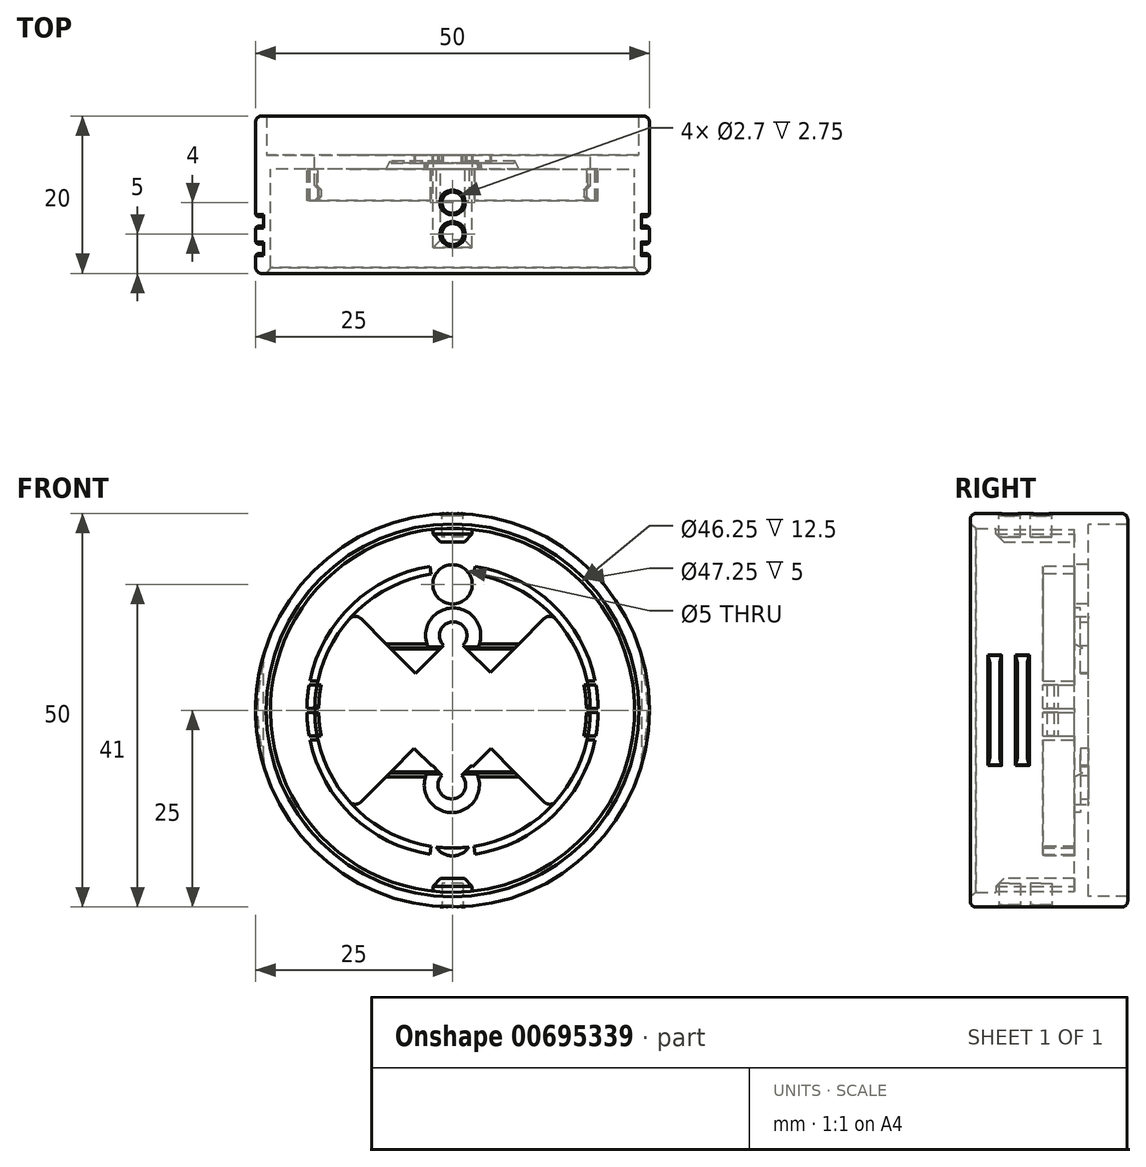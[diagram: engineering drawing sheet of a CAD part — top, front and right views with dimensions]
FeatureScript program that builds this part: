
annotation { "Feature Type Name" : "Feature", "Feature Type Description" : "" }
export const myFeature = defineFeature(function(context is Context, id is Id, definition is map)
    precondition{}
    {
        {
            var Q0;
            Q0=qCreatedBy(makeId("Front.planeOp"),FACE);
            var sketch = newSketch(context, id + "F0", { "sketchPlane" : qUnion([Q0])});
            skCircle(sketch, "E0", {"center": v(0, 0) * mm, "radius": 23.62 * mm});
            skCircle(sketch, "E1", {"center": v(0, 0) * mm, "radius": 25 * mm});
            skArc(sketch, "E2", {"start": v(-12.37, 12.37) * mm, "mid": v(-17.5, 0) * mm, "end": v(-12.37, -12.37) * mm});
            skLineSegment(sketch, "E3.bottom", {"start": v(-1.33, -8.26) * mm, "end": v(-4.8, -4.8) * mm});
            skLineSegment(sketch, "E3.top", {"start": v(4.8, 4.8) * mm, "end": v(1.33, 8.26) * mm});
            skLineSegment(sketch, "E3.left", {"start": v(1.15, -8.26) * mm, "end": v(4.7, -4.7) * mm});
            skLineSegment(sketch, "E3.right", {"start": v(-4.7, 4.7) * mm, "end": v(-1.15, 8.26) * mm});
            skArc(sketch, "E4", {"start": v(1.33, 8.26) * mm, "mid": v(0.1, 11.25) * mm, "end": v(-1.15, 8.26) * mm});
            skArc(sketch, "E5", {"start": v(-1.33, -8.26) * mm, "mid": v(-0.09, -11.25) * mm, "end": v(1.15, -8.26) * mm});
            skLineSegment(sketch, "E6", {"start": v(4.7, -4.7) * mm, "end": v(12.37, -12.37) * mm});
            skLineSegment(sketch, "E7", {"start": v(4.8, 4.8) * mm, "end": v(12.37, 12.37) * mm});
            skLineSegment(sketch, "E8", {"start": v(-4.7, 4.7) * mm, "end": v(-12.37, 12.37) * mm});
            skLineSegment(sketch, "E9", {"start": v(-4.8, -4.8) * mm, "end": v(-12.37, -12.37) * mm});
            skArc(sketch, "E10.trimOffspring", {"start": v(12.37, -12.37) * mm, "mid": v(17.5, 0) * mm, "end": v(12.37, 12.37) * mm});
            skCircle(sketch, "E11", {"center": v(0, 0) * mm, "radius": 23.12 * mm});
            skSolve(sketch);
        }
        {
            var Q0;
            Q0=makeQuery(id+"F0.imprint","IMPRINT",FACE,{"disambiguationData":[TD([[makeQuery(id+"F0.imprint","IMPRINT",EDGE,{"derivedFrom":sQuery(id+"F0.wireOp",EDGE,"E0")}),-1.0]])]});
            var Q1;
            Q1=makeQuery(id+"F0.imprint","IMPRINT",FACE,{"disambiguationData":[TD([[makeQuery(id+"F0.imprint","IMPRINT",EDGE,{"derivedFrom":sQuery(id+"F0.wireOp",EDGE,"E0")}),1.0]])]});
            extrude(context, id + "F1", {"entities" : qUnion([Q0, Q1]), "depth" : 15 * mm, "offsetDistance" : 25 * mm});
        }
        {
            var Q0;
            Q0=makeQuery(id+"F0.imprint","IMPRINT",FACE,{"disambiguationData":[TD([[makeQuery(id+"F0.imprint","IMPRINT",EDGE,{"derivedFrom":sQuery(id+"F0.wireOp",EDGE,"E2")}),-1.0]])]});
            extrude(context, id + "F2", {"entities" : qUnion([Q0]), "operationType" : NewBodyOperationType.ADD, "depth" : 1.75 * mm, "offsetDistance" : 25 * mm});
        }
        {
            var Q0;
            Q0=makeQuery(id+"F0.imprint","IMPRINT",FACE,{"disambiguationData":[TD([[makeQuery(id+"F0.imprint","IMPRINT",EDGE,{"derivedFrom":sQuery(id+"F0.wireOp",EDGE,"E0")}),-1.0]])]});
            extrude(context, id + "F3", {"entities" : qUnion([Q0]), "operationType" : NewBodyOperationType.ADD, "oppositeDirection" : true, "depth" : 5 * mm, "offsetDistance" : 25 * mm});
        }
        {
            var Q0;
            Q0=makeQuery(id+"F2.opExtrude","CAP_FACE",FACE,{"disambiguationData":[OSD([sQuery(id+"F0.wireOp",EDGE,"E0"),sQuery(id+"F0.wireOp",EDGE,"E2"),sQuery(id+"F0.wireOp",EDGE,"E3.bottom"),sQuery(id+"F0.wireOp",EDGE,"E3.top"),sQuery(id+"F0.wireOp",EDGE,"E3.left"),sQuery(id+"F0.wireOp",EDGE,"E3.right"),sQuery(id+"F0.wireOp",EDGE,"E4"),sQuery(id+"F0.wireOp",EDGE,"E5"),sQuery(id+"F0.wireOp",EDGE,"E6"),sQuery(id+"F0.wireOp",EDGE,"E7"),sQuery(id+"F0.wireOp",EDGE,"E8"),sQuery(id+"F0.wireOp",EDGE,"E9"),sQuery(id+"F0.wireOp",EDGE,"E10.trimOffspring")])],"isStart":false});
            var sketch = newSketch(context, id + "F4", { "sketchPlane" : qUnion([Q0])});
            skCircle(sketch, "E12", {"center": v(0.1, 9.5) * mm, "radius": 3.5 * mm});
            skCircle(sketch, "E13", {"center": v(-0.09, -9.5) * mm, "radius": 3.5 * mm});
            skSolve(sketch);
        }
        {
            var Q0;
            Q0 = qSketchRegion(id + "F4", true);
            extrude(context, id + "F5", {"entities" : qUnion([Q0]), "operationType" : NewBodyOperationType.REMOVE, "oppositeDirection" : true, "depth" : .75 * mm, "offsetDistance" : 25 * mm});
        }
        {
            var Q0;
            Q0=makeQuery(id+"F2.opExtrude","CAP_FACE",FACE,{"disambiguationData":[OSD([sQuery(id+"F0.wireOp",EDGE,"E0"),sQuery(id+"F0.wireOp",EDGE,"E2"),sQuery(id+"F0.wireOp",EDGE,"E3.bottom"),sQuery(id+"F0.wireOp",EDGE,"E3.top"),sQuery(id+"F0.wireOp",EDGE,"E3.left"),sQuery(id+"F0.wireOp",EDGE,"E3.right"),sQuery(id+"F0.wireOp",EDGE,"E4"),sQuery(id+"F0.wireOp",EDGE,"E5"),sQuery(id+"F0.wireOp",EDGE,"E6"),sQuery(id+"F0.wireOp",EDGE,"E7"),sQuery(id+"F0.wireOp",EDGE,"E8"),sQuery(id+"F0.wireOp",EDGE,"E9"),sQuery(id+"F0.wireOp",EDGE,"E10.trimOffspring")])],"isStart":false});
            var sketch = newSketch(context, id + "F6", { "sketchPlane" : qUnion([Q0])});
            skCircle(sketch, "E14", {"center": v(0, 0) * mm, "radius": 17.5 * mm});
            skArc(sketch, "E15", {"start": v(18.12, 3.75) * mm, "mid": v(0, 18.5) * mm, "end": v(-18.12, 3.75) * mm});
            skLineSegment(sketch, "E16", {"start": v(-18.21, 3.25) * mm, "end": v(-17.2, 3.25) * mm});
            skLineSegment(sketch, "E17", {"start": v(-18.12, 3.75) * mm, "end": v(-17.1, 3.75) * mm});
            skLineSegment(sketch, "E18.MirrorCS", {"start": v(-18.21, -3.25) * mm, "end": v(-17.2, -3.25) * mm});
            skLineSegment(sketch, "E19.MirrorCS", {"start": v(-18.12, -3.75) * mm, "end": v(-17.1, -3.75) * mm});
            skLineSegment(sketch, "E20.trimOffspring", {"start": v(-17.5, 0.25) * mm, "end": v(-18.5, 0.25) * mm});
            skLineSegment(sketch, "E21.trimOffspring", {"start": v(-17.5, -0.25) * mm, "end": v(-18.5, -0.25) * mm});
            skLineSegment(sketch, "E22", {"start": v(0, 0) * mm, "end": v(0, 1.2) * mm});
            skLineSegment(sketch, "E23.MirrorCS", {"start": v(18.12, 3.75) * mm, "end": v(17.1, 3.75) * mm});
            skLineSegment(sketch, "E24.MirrorCS", {"start": v(18.21, 3.25) * mm, "end": v(17.2, 3.25) * mm});
            skLineSegment(sketch, "E25.MirrorCS", {"start": v(17.5, 0.25) * mm, "end": v(18.5, 0.25) * mm});
            skLineSegment(sketch, "E26.MirrorCS", {"start": v(17.5, -0.25) * mm, "end": v(18.5, -0.25) * mm});
            skLineSegment(sketch, "E27.MirrorCS", {"start": v(18.21, -3.25) * mm, "end": v(17.2, -3.25) * mm});
            skLineSegment(sketch, "E28.MirrorCS", {"start": v(18.12, -3.75) * mm, "end": v(17.1, -3.75) * mm});
            skArc(sketch, "E29.trimOffspring", {"start": v(18.5, 0.25) * mm, "mid": v(18.42, 1.76) * mm, "end": v(18.21, 3.25) * mm});
            skArc(sketch, "E30.trimOffspring", {"start": v(18.21, -3.25) * mm, "mid": v(18.42, -1.76) * mm, "end": v(18.5, -0.25) * mm});
            skArc(sketch, "E31.trimOffspring", {"start": v(-18.21, 3.25) * mm, "mid": v(-18.42, 1.76) * mm, "end": v(-18.5, 0.25) * mm});
            skArc(sketch, "E32.trimOffspring", {"start": v(-18.5, -0.25) * mm, "mid": v(-18.42, -1.76) * mm, "end": v(-18.21, -3.25) * mm});
            skArc(sketch, "E33.trimOffspring", {"start": v(-18.12, -3.75) * mm, "mid": v(0, -18.5) * mm, "end": v(18.12, -3.75) * mm});
            skSolve(sketch);
        }
        {
            var Q0;
            Q0=makeQuery(id+"F6.imprint","IMPRINT",FACE,{"disambiguationData":[TD([[makeQuery(id+"F6.imprint","IMPRINT",EDGE,{"derivedFrom":sQuery(id+"F6.wireOp",EDGE,"E15")}),1.0]])]});
            var Q1;
            {var subQ0=sQuery(id+"F6.wireOp",EDGE,"E24.MirrorCS");Q1=makeQuery(id+"F6.imprint","IMPRINT",FACE,{"disambiguationData":[TD([[makeQuery(id+"F6.imprint","IMPRINT",EDGE,{"derivedFrom":subQ0}),1.0]])]});}
            var Q2;
            {var subQ0=sQuery(id+"F6.wireOp",EDGE,"E26.MirrorCS");Q2=makeQuery(id+"F6.imprint","IMPRINT",FACE,{"disambiguationData":[TD([[makeQuery(id+"F6.imprint","IMPRINT",EDGE,{"derivedFrom":subQ0}),-1.0]])]});}
            var Q3;
            {var subQ0=sQuery(id+"F6.wireOp",EDGE,"E19.MirrorCS");Q3=makeQuery(id+"F6.imprint","IMPRINT",FACE,{"disambiguationData":[TD([[makeQuery(id+"F6.imprint","IMPRINT",EDGE,{"derivedFrom":subQ0}),-1.0]])]});}
            var Q4;
            {var subQ0=sQuery(id+"F6.wireOp",EDGE,"E16");Q4=makeQuery(id+"F6.imprint","IMPRINT",FACE,{"disambiguationData":[TD([[makeQuery(id+"F6.imprint","IMPRINT",EDGE,{"derivedFrom":subQ0}),-1.0]])]});}
            var Q5;
            {var subQ0=sQuery(id+"F6.wireOp",EDGE,"E18.MirrorCS");Q5=makeQuery(id+"F6.imprint","IMPRINT",FACE,{"disambiguationData":[TD([[makeQuery(id+"F6.imprint","IMPRINT",EDGE,{"derivedFrom":subQ0}),1.0]])]});}
            extrude(context, id + "F7", {"entities" : qUnion([Q0, Q1, Q2, Q3, Q4, Q5]), "operationType" : NewBodyOperationType.ADD, "depth" : 4 * mm, "offsetDistance" : 25 * mm});
        }
        {
            var Q0;
            {var subQ11=sQuery(id+"F0.wireOp",EDGE,"E7");var subQ14=sQuery(id+"F0.wireOp",EDGE,"E8");var subQ16=sQuery(id+"F0.wireOp",EDGE,"E2");var subQ17=sQuery(id+"F0.wireOp",EDGE,"E10.trimOffspring");var subQ19=sQuery(id+"F0.wireOp",EDGE,"E11");var subQ20=sQuery(id+"F0.wireOp",EDGE,"E9");var subQ22=sQuery(id+"F0.wireOp",EDGE,"E6");Q0=makeQuery(id+"F7.boolean.opBoolean","SPLIT",FACE,{"disambiguationData":[TD([makeQuery(id+"F1.opExtrude","SWEPT_FACE",FACE,{"disambiguationData":[OSD([subQ19])]})])],"derivedFrom":makeQuery(id+"F2.opExtrude","CAP_FACE",FACE,{"disambiguationData":[OSD([subQ16,sQuery(id+"F0.wireOp",EDGE,"E3.bottom"),sQuery(id+"F0.wireOp",EDGE,"E3.top"),sQuery(id+"F0.wireOp",EDGE,"E3.left"),sQuery(id+"F0.wireOp",EDGE,"E3.right"),sQuery(id+"F0.wireOp",EDGE,"E4"),sQuery(id+"F0.wireOp",EDGE,"E5"),subQ22,subQ11,subQ14,subQ20,subQ17,subQ19])],"isStart":false})});}
            var sketch = newSketch(context, id + "F8", { "sketchPlane" : qUnion([Q0])});
            skLineSegment(sketch, "E34.bottom", {"start": v(2.5, 21.37) * mm, "end": v(-2.5, 21.37) * mm});
            skLineSegment(sketch, "E34.top", {"start": v(2.5, 24.87) * mm, "end": v(-2.5, 24.87) * mm});
            skLineSegment(sketch, "E34.left", {"start": v(2.5, 21.37) * mm, "end": v(2.5, 24.87) * mm});
            skLineSegment(sketch, "E34.right", {"start": v(-2.5, 21.37) * mm, "end": v(-2.5, 24.87) * mm});
            skPoint(sketch, "E34.middle", {"position": v(0, 23.12) * mm});
            skCircle(sketch, "E35", {"center": v(0, 0) * mm, "radius": 23.12 * mm});
            skLineSegment(sketch, "E36", {"start": v(0, 0) * mm, "end": v(4.23, 0) * mm});
            skLineSegment(sketch, "E37.MirrorCS", {"start": v(-7.5, 21.37) * mm, "end": v(-2.5, 21.37) * mm});
            skLineSegment(sketch, "E38.MirrorCS", {"start": v(-7.5, 21.37) * mm, "end": v(-7.5, 24.87) * mm});
            skLineSegment(sketch, "E39.MirrorCS", {"start": v(-2.5, -21.37) * mm, "end": v(-2.5, -24.87) * mm});
            skLineSegment(sketch, "E40.MirrorCS", {"start": v(2.5, -21.37) * mm, "end": v(2.5, -24.87) * mm});
            skLineSegment(sketch, "E41.MirrorCS", {"start": v(2.5, -21.37) * mm, "end": v(-2.5, -21.37) * mm});
            skLineSegment(sketch, "E42.MirrorCS", {"start": v(2.5, -24.87) * mm, "end": v(-2.5, -24.87) * mm});
            skSolve(sketch);
        }
        {
            var Q0;
            {var subQ0=sQuery(id+"F8.wireOp",EDGE,"E34.bottom");Q0=makeQuery(id+"F8.imprint","IMPRINT",FACE,{"disambiguationData":[TD([[makeQuery(id+"F8.imprint","IMPRINT",EDGE,{"derivedFrom":subQ0}),-1.0]])]});}
            var Q1;
            {var subQ5=sQuery(id+"F8.wireOp",EDGE,"E41.MirrorCS");Q1=makeQuery(id+"F8.imprint","IMPRINT",FACE,{"disambiguationData":[TD([[makeQuery(id+"F8.imprint","IMPRINT",EDGE,{"derivedFrom":subQ5}),1.0]])]});}
            extrude(context, id + "F9", {"entities" : qUnion([Q0, Q1]), "operationType" : NewBodyOperationType.ADD, "depth" : 10 * mm, "offsetDistance" : 25 * mm});
        }
        {
            var Q0;
            Q0=makeQuery(id+"F2.opExtrude","CAP_FACE",FACE,{"disambiguationData":[OSD([sQuery(id+"F0.wireOp",EDGE,"E0"),sQuery(id+"F0.wireOp",EDGE,"E2"),sQuery(id+"F0.wireOp",EDGE,"E3.bottom"),sQuery(id+"F0.wireOp",EDGE,"E3.top"),sQuery(id+"F0.wireOp",EDGE,"E3.left"),sQuery(id+"F0.wireOp",EDGE,"E3.right"),sQuery(id+"F0.wireOp",EDGE,"E4"),sQuery(id+"F0.wireOp",EDGE,"E5"),sQuery(id+"F0.wireOp",EDGE,"E6"),sQuery(id+"F0.wireOp",EDGE,"E7"),sQuery(id+"F0.wireOp",EDGE,"E8"),sQuery(id+"F0.wireOp",EDGE,"E9"),sQuery(id+"F0.wireOp",EDGE,"E10.trimOffspring")])],"isStart":false});
            var sketch = newSketch(context, id + "F10", { "sketchPlane" : qUnion([Q0])});
            skLineSegment(sketch, "E43.bottom", {"start": v(9.72, 0) * mm, "end": v(0, -9.72) * mm});
            skLineSegment(sketch, "E43.top", {"start": v(0, 9.72) * mm, "end": v(-9.72, 0) * mm});
            skLineSegment(sketch, "E43.left", {"start": v(9.72, 0) * mm, "end": v(0, 9.72) * mm});
            skLineSegment(sketch, "E43.right", {"start": v(0, -9.72) * mm, "end": v(-9.72, 0) * mm});
            skPoint(sketch, "E43.middle", {"position": v(0, 0) * mm});
            skSolve(sketch);
        }
        {
            var Q0;
            Q0=makeQuery(id+"F7.opExtrude","CAP_FACE",FACE,{"disambiguationData":[OSD([sQuery(id+"F6.wireOp",EDGE,"E14"),sQuery(id+"F6.wireOp",EDGE,"E15"),sQuery(id+"F6.wireOp",EDGE,"E17"),sQuery(id+"F6.wireOp",EDGE,"E23.MirrorCS")])],"isStart":false});
            var sketch = newSketch(context, id + "F11", { "sketchPlane" : qUnion([Q0])});
            skArc(sketch, "E44", {"start": v(-16.69, 3.25) * mm, "mid": v(-16.9, 1.76) * mm, "end": v(-17, 0.25) * mm});
            skLineSegment(sketch, "E45", {"start": v(-17.7, 3.25) * mm, "end": v(-16.69, 3.25) * mm});
            skLineSegment(sketch, "E46", {"start": v(-18, 0.25) * mm, "end": v(-17, 0.25) * mm});
            skLineSegment(sketch, "E47", {"start": v(-18, -0.25) * mm, "end": v(-17, -0.25) * mm});
            skLineSegment(sketch, "E48", {"start": v(-17.7, -3.25) * mm, "end": v(-16.69, -3.25) * mm});
            skArc(sketch, "E49.trimOffspring", {"start": v(-17, -0.25) * mm, "mid": v(-16.9, -1.76) * mm, "end": v(-16.69, -3.25) * mm});
            skLineSegment(sketch, "E50", {"start": v(0, 0) * mm, "end": v(0, 1.46) * mm});
            skLineSegment(sketch, "E51.MirrorCS", {"start": v(18, -0.25) * mm, "end": v(17, -0.25) * mm});
            skLineSegment(sketch, "E52.MirrorCS", {"start": v(17.7, -3.25) * mm, "end": v(16.69, -3.25) * mm});
            skLineSegment(sketch, "E53.MirrorCS", {"start": v(18, 0.25) * mm, "end": v(17, 0.25) * mm});
            skArc(sketch, "E54.MirrorCS", {"start": v(17.7, 3.25) * mm, "mid": v(17.91, 1.76) * mm, "end": v(18, 0.25) * mm});
            skArc(sketch, "E55.MirrorCS", {"start": v(16.69, 3.25) * mm, "mid": v(16.9, 1.76) * mm, "end": v(17, 0.25) * mm});
            skArc(sketch, "E56.MirrorCS", {"start": v(18, -0.25) * mm, "mid": v(17.92, -1.76) * mm, "end": v(17.7, -3.25) * mm});
            skLineSegment(sketch, "E57.MirrorCS", {"start": v(17.7, 3.25) * mm, "end": v(16.69, 3.25) * mm});
            skArc(sketch, "E58.MirrorCS", {"start": v(17, -0.25) * mm, "mid": v(16.9, -1.76) * mm, "end": v(16.69, -3.25) * mm});
            skLineSegment(sketch, "E59", {"start": v(-17.7, 3.25) * mm, "end": v(-18, 0.25) * mm});
            skLineSegment(sketch, "E60", {"start": v(-18, -0.25) * mm, "end": v(-17.7, -3.25) * mm});
            skLineSegment(sketch, "E61.MirrorCS", {"start": v(18, -0.25) * mm, "end": v(17.7, -3.25) * mm});
            skLineSegment(sketch, "E62.MirrorCS", {"start": v(17.7, 3.25) * mm, "end": v(18, 0.25) * mm});
            skSolve(sketch);
        }
        {
            var Q0;
            Q0=makeQuery(id+"F11.imprint","IMPRINT",FACE,{"disambiguationData":[TD([[makeQuery(id+"F11.imprint","IMPRINT",EDGE,{"derivedFrom":sQuery(id+"F11.wireOp",EDGE,"E47")}),-1.0]])]});
            var Q1;
            Q1=makeQuery(id+"F11.imprint","IMPRINT",FACE,{"disambiguationData":[TD([[makeQuery(id+"F11.imprint","IMPRINT",EDGE,{"derivedFrom":sQuery(id+"F11.wireOp",EDGE,"E44")}),-1.0]])]});
            var Q2;
            Q2=makeQuery(id+"F11.imprint","IMPRINT",FACE,{"disambiguationData":[TD([[makeQuery(id+"F11.imprint","IMPRINT",EDGE,{"derivedFrom":sQuery(id+"F11.wireOp",EDGE,"E57.MirrorCS")}),1.0]])]});
            var Q3;
            Q3=makeQuery(id+"F11.imprint","IMPRINT",FACE,{"disambiguationData":[TD([[makeQuery(id+"F11.imprint","IMPRINT",EDGE,{"derivedFrom":sQuery(id+"F11.wireOp",EDGE,"E52.MirrorCS")}),-1.0]])]});
            extrude(context, id + "F12", {"entities" : qUnion([Q0, Q1, Q2, Q3]), "operationType" : NewBodyOperationType.ADD, "oppositeDirection" : true, "depth" : 1.9 * mm, "offsetDistance" : 25 * mm});
        }
        {
            var Q0;
            Q0=makeQuery(id+"F12.opExtrude","CAP_EDGE",EDGE,{"disambiguationData":[OSD([sQuery(id+"F11.wireOp",EDGE,"E44")])],"isStart":true});
            var Q1;
            Q1=makeQuery(id+"F12.opExtrude","CAP_EDGE",EDGE,{"disambiguationData":[OSD([sQuery(id+"F11.wireOp",EDGE,"E49.trimOffspring")])],"isStart":true});
            var Q2;
            Q2=makeQuery(id+"F12.opExtrude","CAP_EDGE",EDGE,{"disambiguationData":[OSD([sQuery(id+"F11.wireOp",EDGE,"E55.MirrorCS")])],"isStart":true});
            var Q3;
            Q3=makeQuery(id+"F12.opExtrude","CAP_EDGE",EDGE,{"disambiguationData":[OSD([sQuery(id+"F11.wireOp",EDGE,"E58.MirrorCS")])],"isStart":true});
            chamfer(context, id + "F13", {"entities" : qUnion([Q0, Q1, Q2, Q3]), "width" : .5 * mm, "tangentPropagation" : true});
        }
        {
            var Q0;
            Q0=makeQuery(id+"F12.opExtrude","CAP_EDGE",EDGE,{"disambiguationData":[OSD([sQuery(id+"F11.wireOp",EDGE,"E44")])],"isStart":false});
            var Q1;
            Q1=makeQuery(id+"F12.opExtrude","CAP_EDGE",EDGE,{"disambiguationData":[OSD([sQuery(id+"F11.wireOp",EDGE,"E49.trimOffspring")])],"isStart":false});
            var Q2;
            Q2=makeQuery(id+"F12.opExtrude","CAP_EDGE",EDGE,{"disambiguationData":[OSD([sQuery(id+"F11.wireOp",EDGE,"E55.MirrorCS")])],"isStart":false});
            var Q3;
            Q3=makeQuery(id+"F12.opExtrude","CAP_EDGE",EDGE,{"disambiguationData":[OSD([sQuery(id+"F11.wireOp",EDGE,"E58.MirrorCS")])],"isStart":false});
            chamfer(context, id + "F14", {"entities" : qUnion([Q0, Q1, Q2, Q3]), "width" : .5 * mm, "tangentPropagation" : true});
        }
        {
            var Q0;
            Q0=qCreatedBy(makeId("Top.planeOp"),FACE);
            cPlane(context, id + "F15", {"entities" : qUnion([Q0]), "cplaneType" : CPlaneType.OFFSET, "offset" : 25 * mm, "width" : 150 * mm, "height" : 150 * mm});
        }
        {
            var Q0;
            Q0=makeQuery(id+"F1.opExtrude","CAP_FACE",FACE,{"disambiguationData":[OSD([sQuery(id+"F0.wireOp",EDGE,"E0"),sQuery(id+"F0.wireOp",EDGE,"E1")])],"isStart":false});
            var sketch = newSketch(context, id + "F16", { "sketchPlane" : qUnion([Q0])});
            skPoint(sketch, "E63", {"position": v(0, 0) * mm});
            skSolve(sketch);
        }
        {
            var Q0;
            Q0=qCreatedBy(id+"F15.planeOp",FACE);
            var sketch = newSketch(context, id + "F17", { "sketchPlane" : qUnion([Q0])});
            skLineSegment(sketch, "E64", {"start": v(0, -15) * mm, "end": v(0, -10) * mm});
            skCircle(sketch, "E65", {"center": v(0, -10) * mm, "radius": 1.35 * mm});
            skLineSegment(sketch, "E66", {"start": v(0, -15) * mm, "end": v(0, -6) * mm});
            skCircle(sketch, "E67", {"center": v(0, -6) * mm, "radius": 1.35 * mm});
            skSolve(sketch);
        }
        {
            var Q0;
            Q0 = qSketchRegion(id + "F17", true);
            extrude(context, id + "F18", {"entities" : qUnion([Q0]), "operationType" : NewBodyOperationType.REMOVE, "oppositeDirection" : true, "depth" : 3 * mm, "offsetDistance" : 25 * mm});
        }
        {
            var Q0;
            Q0=qCreatedBy(makeId("Top.planeOp"),FACE);
            cPlane(context, id + "F19", {"entities" : qUnion([Q0]), "cplaneType" : CPlaneType.OFFSET, "offset" : 25 * mm, "oppositeDirection" : true, "width" : 150 * mm, "height" : 150 * mm});
        }
        {
            var Q0;
            Q0=qCreatedBy(id+"F19.planeOp",FACE);
            var sketch = newSketch(context, id + "F20", { "sketchPlane" : qUnion([Q0])});
            skLineSegment(sketch, "E68", {"start": v(0, -15) * mm, "end": v(0, -10) * mm});
            skCircle(sketch, "E69", {"center": v(0, -10) * mm, "radius": 1.35 * mm});
            skLineSegment(sketch, "E70", {"start": v(0, -15) * mm, "end": v(0, -6) * mm});
            skCircle(sketch, "E71", {"center": v(0, -6) * mm, "radius": 1.35 * mm});
            skSolve(sketch);
        }
        {
            var Q0;
            Q0 = qSketchRegion(id + "F20", true);
            extrude(context, id + "F21", {"entities" : qUnion([Q0]), "operationType" : NewBodyOperationType.REMOVE, "depth" : 3 * mm, "offsetDistance" : 25 * mm});
        }
        {
            var Q0;
            Q0=qCreatedBy(makeId("Right.planeOp"),FACE);
            cPlane(context, id + "F22", {"entities" : qUnion([Q0]), "cplaneType" : CPlaneType.OFFSET, "offset" : 25 * mm, "width" : 150 * mm, "height" : 150 * mm});
        }
        {
            var Q0;
            Q0=qCreatedBy(id+"F22.planeOp",FACE);
            var sketch = newSketch(context, id + "F23", { "sketchPlane" : qUnion([Q0])});
            skLineSegment(sketch, "E72", {"start": v(-15, 0) * mm, "end": v(-11.88, 0) * mm});
            skLineSegment(sketch, "E73.bottom", {"start": v(-11.26, -25) * mm, "end": v(-12.5, -25) * mm});
            skLineSegment(sketch, "E73.top", {"start": v(-11.25, 25) * mm, "end": v(-12.5, 25) * mm});
            skLineSegment(sketch, "E73.left", {"start": v(-11.26, -25) * mm, "end": v(-11.25, 25) * mm});
            skLineSegment(sketch, "E73.right", {"start": v(-12.5, -25) * mm, "end": v(-12.5, 25) * mm});
            skPoint(sketch, "E73.middle", {"position": v(-11.88, 0) * mm});
            skLineSegment(sketch, "E74.bottom", {"start": v(-9, 25) * mm, "end": v(-7.75, 25) * mm});
            skLineSegment(sketch, "E74.top", {"start": v(-9, -25) * mm, "end": v(-7.75, -25) * mm});
            skLineSegment(sketch, "E74.left", {"start": v(-9, 25) * mm, "end": v(-9, -25) * mm});
            skLineSegment(sketch, "E74.right", {"start": v(-7.75, 25) * mm, "end": v(-7.75, -25) * mm});
            skPoint(sketch, "E74.middle", {"position": v(-8.38, 0) * mm});
            skSolve(sketch);
        }
        {
            var Q0;
            Q0 = qSketchRegion(id + "F23", true);
            extrude(context, id + "F24", {"entities" : qUnion([Q0]), "operationType" : NewBodyOperationType.REMOVE, "oppositeDirection" : true, "depth" : 1 * mm, "offsetDistance" : 25 * mm});
        }
        {
            var Q0;
            Q0=qCreatedBy(makeId("Right.planeOp"),FACE);
            cPlane(context, id + "F25", {"entities" : qUnion([Q0]), "cplaneType" : CPlaneType.OFFSET, "offset" : 25 * mm, "oppositeDirection" : true, "width" : 150 * mm, "height" : 150 * mm});
        }
        {
            var Q0;
            Q0=qCreatedBy(id+"F25.planeOp",FACE);
            var sketch = newSketch(context, id + "F26", { "sketchPlane" : qUnion([Q0])});
            skLineSegment(sketch, "E75", {"start": v(-15, 0) * mm, "end": v(-11.88, 0) * mm});
            skLineSegment(sketch, "E76.bottom", {"start": v(-9, -25) * mm, "end": v(-7.76, -25) * mm});
            skLineSegment(sketch, "E76.top", {"start": v(-9, 25) * mm, "end": v(-7.75, 25) * mm});
            skLineSegment(sketch, "E76.left", {"start": v(-9, -25) * mm, "end": v(-9, 25) * mm});
            skLineSegment(sketch, "E76.right", {"start": v(-7.76, -25) * mm, "end": v(-7.75, 25) * mm});
            skPoint(sketch, "E76.middle", {"position": v(-8.38, 0) * mm});
            skLineSegment(sketch, "E77.bottom", {"start": v(-12.5, -25) * mm, "end": v(-11.26, -25) * mm});
            skLineSegment(sketch, "E77.top", {"start": v(-12.5, 25) * mm, "end": v(-11.25, 25) * mm});
            skLineSegment(sketch, "E77.left", {"start": v(-12.5, -25) * mm, "end": v(-12.5, 25) * mm});
            skLineSegment(sketch, "E77.right", {"start": v(-11.26, -25) * mm, "end": v(-11.25, 25) * mm});
            skPoint(sketch, "E77.middle", {"position": v(-11.88, 0) * mm});
            skSolve(sketch);
        }
        {
            var Q0;
            Q0 = qSketchRegion(id + "F26", true);
            extrude(context, id + "F27", {"entities" : qUnion([Q0]), "operationType" : NewBodyOperationType.REMOVE, "depth" : 1 * mm, "offsetDistance" : 25 * mm});
        }
        {
            var Q0;
            Q0=makeQuery(id+"F40.boolean.opBoolean","INTERSECT",EDGE,{"derivedFrom":[makeQuery(id+"F2.opExtrude","SWEPT_FACE",FACE,{"disambiguationData":[OSD([sQuery(id+"F0.wireOp",EDGE,"E8")])]}),makeQuery(id+"F40.opExtrude","SWEPT_FACE",FACE,{"disambiguationData":[OSD([sQuery(id+"F10.wireOp",EDGE,"E43.top")])]})]});
            var Q1;
            Q1=makeQuery(id+"F40.boolean.opBoolean","INTERSECT",EDGE,{"derivedFrom":[makeQuery(id+"F2.opExtrude","SWEPT_FACE",FACE,{"disambiguationData":[OSD([sQuery(id+"F0.wireOp",EDGE,"E7")])]}),makeQuery(id+"F40.opExtrude","SWEPT_FACE",FACE,{"disambiguationData":[OSD([sQuery(id+"F10.wireOp",EDGE,"E43.left")])]})]});
            var Q2;
            Q2=makeQuery(id+"F40.boolean.opBoolean","INTERSECT",EDGE,{"derivedFrom":[makeQuery(id+"F2.opExtrude","SWEPT_FACE",FACE,{"disambiguationData":[OSD([sQuery(id+"F0.wireOp",EDGE,"E6")])]}),makeQuery(id+"F40.opExtrude","SWEPT_FACE",FACE,{"disambiguationData":[OSD([sQuery(id+"F10.wireOp",EDGE,"E43.bottom")])]})]});
            var Q3;
            Q3=makeQuery(id+"F40.boolean.opBoolean","INTERSECT",EDGE,{"derivedFrom":[makeQuery(id+"F2.opExtrude","SWEPT_FACE",FACE,{"disambiguationData":[OSD([sQuery(id+"F0.wireOp",EDGE,"E9")])]}),makeQuery(id+"F40.opExtrude","SWEPT_FACE",FACE,{"disambiguationData":[OSD([sQuery(id+"F10.wireOp",EDGE,"E43.right")])]})]});
            var Q4;
            Q4=makeQuery(id+"F2.opExtrude","SWEPT_EDGE",EDGE,{"disambiguationData":[OSD([sQuery(id+"F0.wireOp",EDGE,"E6"),sQuery(id+"F0.wireOp",EDGE,"E10.trimOffspring")])]});
            var Q5;
            Q5=makeQuery(id+"F2.opExtrude","SWEPT_EDGE",EDGE,{"disambiguationData":[OSD([sQuery(id+"F0.wireOp",EDGE,"E7"),sQuery(id+"F0.wireOp",EDGE,"E10.trimOffspring")])]});
            var Q6;
            Q6=makeQuery(id+"F2.opExtrude","SWEPT_EDGE",EDGE,{"disambiguationData":[OSD([sQuery(id+"F0.wireOp",EDGE,"E2"),sQuery(id+"F0.wireOp",EDGE,"E8")])]});
            var Q7;
            Q7=makeQuery(id+"F2.opExtrude","SWEPT_EDGE",EDGE,{"disambiguationData":[OSD([sQuery(id+"F0.wireOp",EDGE,"E2"),sQuery(id+"F0.wireOp",EDGE,"E9")])]});
            fillet(context, id + "F28", {"entities" : qUnion([Q0, Q1, Q2, Q3, Q4, Q5, Q6, Q7]), "radius" : 1 * mm, "tangentPropagation" : true, "allowEdgeOverflow" : false});
        }
        {
            var Q0;
            Q0=makeQuery(id+"F1.opExtrude","CAP_EDGE",EDGE,{"disambiguationData":[OSD([sQuery(id+"F0.wireOp",EDGE,"E1")])],"isStart":false});
            var Q1;
            Q1=makeQuery(id+"F3.opExtrude","CAP_EDGE",EDGE,{"disambiguationData":[OSD([sQuery(id+"F0.wireOp",EDGE,"E1")])],"isStart":false});
            fillet(context, id + "F29", {"entities" : qUnion([Q0, Q1]), "radius" : .75 * mm, "tangentPropagation" : true, "allowEdgeOverflow" : false});
        }
        {
            var Q0;
            {var subQ0=sQuery(id+"F0.wireOp",EDGE,"E1");Q0=makeQuery(id+"F27.boolean.opBoolean","INTERSECT",EDGE,{"derivedFrom":[makeQuery(id+"F0lZXDNJsSuf2Zf_1.boolean.opBoolean","SPLIT",FACE,{"disambiguationData":[TD([makeQuery(id+"F0lZXDNJsSuf2Zf_1.opExtrude","SWEPT_FACE",FACE,{"disambiguationData":[OSD([sQuery(id+"Fl6joLbU86pnRP5_1.wireOp",EDGE,"838e0230-e5e1-4c86-9a61-0dafe3e3d36a.sketch_text.stroke-0")])]})])],"derivedFrom":makeQuery(id+"F3.boolean.opBoolean","MERGE",FACE,{"derivedFrom":[makeQuery(id+"F1.opExtrude","SWEPT_FACE",FACE,{"disambiguationData":[OSD([subQ0])]}),makeQuery(id+"F3.opExtrude","SWEPT_FACE",FACE,{"disambiguationData":[OSD([subQ0])]})]})}),makeQuery(id+"F27.opExtrude","SWEPT_FACE",FACE,{"disambiguationData":[OSD([sQuery(id+"F26.wireOp",EDGE,"E76.right")])]})]});}
            var Q1;
            {var subQ0=sQuery(id+"F0.wireOp",EDGE,"E1");Q1=makeQuery(id+"F27.boolean.opBoolean","INTERSECT",EDGE,{"derivedFrom":[makeQuery(id+"F0lZXDNJsSuf2Zf_1.boolean.opBoolean","SPLIT",FACE,{"disambiguationData":[TD([makeQuery(id+"F0lZXDNJsSuf2Zf_1.opExtrude","SWEPT_FACE",FACE,{"disambiguationData":[OSD([sQuery(id+"Fl6joLbU86pnRP5_1.wireOp",EDGE,"838e0230-e5e1-4c86-9a61-0dafe3e3d36a.sketch_text.stroke-0")])]})])],"derivedFrom":makeQuery(id+"F3.boolean.opBoolean","MERGE",FACE,{"derivedFrom":[makeQuery(id+"F1.opExtrude","SWEPT_FACE",FACE,{"disambiguationData":[OSD([subQ0])]}),makeQuery(id+"F3.opExtrude","SWEPT_FACE",FACE,{"disambiguationData":[OSD([subQ0])]})]})}),makeQuery(id+"F27.opExtrude","SWEPT_FACE",FACE,{"disambiguationData":[OSD([sQuery(id+"F26.wireOp",EDGE,"E76.left")])]})]});}
            var Q2;
            {var subQ0=sQuery(id+"F0.wireOp",EDGE,"E1");Q2=makeQuery(id+"F27.boolean.opBoolean","INTERSECT",EDGE,{"derivedFrom":[makeQuery(id+"F0lZXDNJsSuf2Zf_1.boolean.opBoolean","SPLIT",FACE,{"disambiguationData":[TD([makeQuery(id+"F0lZXDNJsSuf2Zf_1.opExtrude","SWEPT_FACE",FACE,{"disambiguationData":[OSD([sQuery(id+"Fl6joLbU86pnRP5_1.wireOp",EDGE,"838e0230-e5e1-4c86-9a61-0dafe3e3d36a.sketch_text.stroke-0")])]})])],"derivedFrom":makeQuery(id+"F3.boolean.opBoolean","MERGE",FACE,{"derivedFrom":[makeQuery(id+"F1.opExtrude","SWEPT_FACE",FACE,{"disambiguationData":[OSD([subQ0])]}),makeQuery(id+"F3.opExtrude","SWEPT_FACE",FACE,{"disambiguationData":[OSD([subQ0])]})]})}),makeQuery(id+"F27.opExtrude","SWEPT_FACE",FACE,{"disambiguationData":[OSD([sQuery(id+"F26.wireOp",EDGE,"E77.right")])]})]});}
            var Q3;
            {var subQ0=sQuery(id+"F0.wireOp",EDGE,"E1");Q3=makeQuery(id+"F27.boolean.opBoolean","INTERSECT",EDGE,{"derivedFrom":[makeQuery(id+"F0lZXDNJsSuf2Zf_1.boolean.opBoolean","SPLIT",FACE,{"disambiguationData":[TD([makeQuery(id+"F0lZXDNJsSuf2Zf_1.opExtrude","SWEPT_FACE",FACE,{"disambiguationData":[OSD([sQuery(id+"Fl6joLbU86pnRP5_1.wireOp",EDGE,"838e0230-e5e1-4c86-9a61-0dafe3e3d36a.sketch_text.stroke-0")])]})])],"derivedFrom":makeQuery(id+"F3.boolean.opBoolean","MERGE",FACE,{"derivedFrom":[makeQuery(id+"F1.opExtrude","SWEPT_FACE",FACE,{"disambiguationData":[OSD([subQ0])]}),makeQuery(id+"F3.opExtrude","SWEPT_FACE",FACE,{"disambiguationData":[OSD([subQ0])]})]})}),makeQuery(id+"F27.opExtrude","SWEPT_FACE",FACE,{"disambiguationData":[OSD([sQuery(id+"F26.wireOp",EDGE,"E77.left")])]})]});}
            var Q4;
            {var subQ0=sQuery(id+"F0.wireOp",EDGE,"E1");Q4=makeQuery(id+"F27.boolean.opBoolean","INTERSECT",EDGE,{"disambiguationData":[OD(0.0)],"derivedFrom":[makeQuery(id+"F0lZXDNJsSuf2Zf_1.boolean.opBoolean","SPLIT",FACE,{"disambiguationData":[TD([makeQuery(id+"F0lZXDNJsSuf2Zf_1.opExtrude","SWEPT_FACE",FACE,{"disambiguationData":[OSD([sQuery(id+"Fl6joLbU86pnRP5_1.wireOp",EDGE,"838e0230-e5e1-4c86-9a61-0dafe3e3d36a.sketch_text.stroke-0")])]})])],"derivedFrom":makeQuery(id+"F3.boolean.opBoolean","MERGE",FACE,{"derivedFrom":[makeQuery(id+"F1.opExtrude","SWEPT_FACE",FACE,{"disambiguationData":[OSD([subQ0])]}),makeQuery(id+"F3.opExtrude","SWEPT_FACE",FACE,{"disambiguationData":[OSD([subQ0])]})]})}),makeQuery(id+"F27.opExtrude","CAP_FACE",FACE,{"disambiguationData":[OSD([sQuery(id+"F26.wireOp",EDGE,"E77.bottom"),sQuery(id+"F26.wireOp",EDGE,"E77.top"),sQuery(id+"F26.wireOp",EDGE,"E77.left"),sQuery(id+"F26.wireOp",EDGE,"E77.right")])],"isStart":false})]});}
            var Q5;
            {var subQ0=sQuery(id+"F0.wireOp",EDGE,"E1");Q5=makeQuery(id+"F27.boolean.opBoolean","INTERSECT",EDGE,{"disambiguationData":[OD(0.0)],"derivedFrom":[makeQuery(id+"F0lZXDNJsSuf2Zf_1.boolean.opBoolean","SPLIT",FACE,{"disambiguationData":[TD([makeQuery(id+"F0lZXDNJsSuf2Zf_1.opExtrude","SWEPT_FACE",FACE,{"disambiguationData":[OSD([sQuery(id+"Fl6joLbU86pnRP5_1.wireOp",EDGE,"838e0230-e5e1-4c86-9a61-0dafe3e3d36a.sketch_text.stroke-0")])]})])],"derivedFrom":makeQuery(id+"F3.boolean.opBoolean","MERGE",FACE,{"derivedFrom":[makeQuery(id+"F1.opExtrude","SWEPT_FACE",FACE,{"disambiguationData":[OSD([subQ0])]}),makeQuery(id+"F3.opExtrude","SWEPT_FACE",FACE,{"disambiguationData":[OSD([subQ0])]})]})}),makeQuery(id+"F27.opExtrude","CAP_FACE",FACE,{"disambiguationData":[OSD([sQuery(id+"F26.wireOp",EDGE,"E76.bottom"),sQuery(id+"F26.wireOp",EDGE,"E76.top"),sQuery(id+"F26.wireOp",EDGE,"E76.left"),sQuery(id+"F26.wireOp",EDGE,"E76.right")])],"isStart":false})]});}
            var Q6;
            {var subQ0=sQuery(id+"F0.wireOp",EDGE,"E1");Q6=makeQuery(id+"F27.boolean.opBoolean","INTERSECT",EDGE,{"disambiguationData":[OD(1.0)],"derivedFrom":[makeQuery(id+"F0lZXDNJsSuf2Zf_1.boolean.opBoolean","SPLIT",FACE,{"disambiguationData":[TD([makeQuery(id+"F0lZXDNJsSuf2Zf_1.opExtrude","SWEPT_FACE",FACE,{"disambiguationData":[OSD([sQuery(id+"Fl6joLbU86pnRP5_1.wireOp",EDGE,"838e0230-e5e1-4c86-9a61-0dafe3e3d36a.sketch_text.stroke-0")])]})])],"derivedFrom":makeQuery(id+"F3.boolean.opBoolean","MERGE",FACE,{"derivedFrom":[makeQuery(id+"F1.opExtrude","SWEPT_FACE",FACE,{"disambiguationData":[OSD([subQ0])]}),makeQuery(id+"F3.opExtrude","SWEPT_FACE",FACE,{"disambiguationData":[OSD([subQ0])]})]})}),makeQuery(id+"F27.opExtrude","CAP_FACE",FACE,{"disambiguationData":[OSD([sQuery(id+"F26.wireOp",EDGE,"E76.bottom"),sQuery(id+"F26.wireOp",EDGE,"E76.top"),sQuery(id+"F26.wireOp",EDGE,"E76.left"),sQuery(id+"F26.wireOp",EDGE,"E76.right")])],"isStart":false})]});}
            var Q7;
            {var subQ0=sQuery(id+"F0.wireOp",EDGE,"E1");Q7=makeQuery(id+"F27.boolean.opBoolean","INTERSECT",EDGE,{"disambiguationData":[OD(1.0)],"derivedFrom":[makeQuery(id+"F0lZXDNJsSuf2Zf_1.boolean.opBoolean","SPLIT",FACE,{"disambiguationData":[TD([makeQuery(id+"F0lZXDNJsSuf2Zf_1.opExtrude","SWEPT_FACE",FACE,{"disambiguationData":[OSD([sQuery(id+"Fl6joLbU86pnRP5_1.wireOp",EDGE,"838e0230-e5e1-4c86-9a61-0dafe3e3d36a.sketch_text.stroke-0")])]})])],"derivedFrom":makeQuery(id+"F3.boolean.opBoolean","MERGE",FACE,{"derivedFrom":[makeQuery(id+"F1.opExtrude","SWEPT_FACE",FACE,{"disambiguationData":[OSD([subQ0])]}),makeQuery(id+"F3.opExtrude","SWEPT_FACE",FACE,{"disambiguationData":[OSD([subQ0])]})]})}),makeQuery(id+"F27.opExtrude","CAP_FACE",FACE,{"disambiguationData":[OSD([sQuery(id+"F26.wireOp",EDGE,"E77.bottom"),sQuery(id+"F26.wireOp",EDGE,"E77.top"),sQuery(id+"F26.wireOp",EDGE,"E77.left"),sQuery(id+"F26.wireOp",EDGE,"E77.right")])],"isStart":false})]});}
            var Q8;
            {var subQ0=sQuery(id+"F0.wireOp",EDGE,"E1");Q8=makeQuery(id+"F24.boolean.opBoolean","INTERSECT",EDGE,{"derivedFrom":[makeQuery(id+"F0lZXDNJsSuf2Zf_1.boolean.opBoolean","SPLIT",FACE,{"disambiguationData":[TD([makeQuery(id+"F0lZXDNJsSuf2Zf_1.opExtrude","SWEPT_FACE",FACE,{"disambiguationData":[OSD([sQuery(id+"Fl6joLbU86pnRP5_1.wireOp",EDGE,"838e0230-e5e1-4c86-9a61-0dafe3e3d36a.sketch_text.stroke-0")])]})])],"derivedFrom":makeQuery(id+"F3.boolean.opBoolean","MERGE",FACE,{"derivedFrom":[makeQuery(id+"F1.opExtrude","SWEPT_FACE",FACE,{"disambiguationData":[OSD([subQ0])]}),makeQuery(id+"F3.opExtrude","SWEPT_FACE",FACE,{"disambiguationData":[OSD([subQ0])]})]})}),makeQuery(id+"F24.opExtrude","SWEPT_FACE",FACE,{"disambiguationData":[OSD([sQuery(id+"F23.wireOp",EDGE,"E73.right")])]})]});}
            var Q9;
            {var subQ0=sQuery(id+"F0.wireOp",EDGE,"E1");Q9=makeQuery(id+"F24.boolean.opBoolean","INTERSECT",EDGE,{"derivedFrom":[makeQuery(id+"F0lZXDNJsSuf2Zf_1.boolean.opBoolean","SPLIT",FACE,{"disambiguationData":[TD([makeQuery(id+"F0lZXDNJsSuf2Zf_1.opExtrude","SWEPT_FACE",FACE,{"disambiguationData":[OSD([sQuery(id+"Fl6joLbU86pnRP5_1.wireOp",EDGE,"838e0230-e5e1-4c86-9a61-0dafe3e3d36a.sketch_text.stroke-0")])]})])],"derivedFrom":makeQuery(id+"F3.boolean.opBoolean","MERGE",FACE,{"derivedFrom":[makeQuery(id+"F1.opExtrude","SWEPT_FACE",FACE,{"disambiguationData":[OSD([subQ0])]}),makeQuery(id+"F3.opExtrude","SWEPT_FACE",FACE,{"disambiguationData":[OSD([subQ0])]})]})}),makeQuery(id+"F24.opExtrude","SWEPT_FACE",FACE,{"disambiguationData":[OSD([sQuery(id+"F23.wireOp",EDGE,"E73.left")])]})]});}
            var Q10;
            {var subQ0=sQuery(id+"F0.wireOp",EDGE,"E1");Q10=makeQuery(id+"F24.boolean.opBoolean","INTERSECT",EDGE,{"derivedFrom":[makeQuery(id+"F0lZXDNJsSuf2Zf_1.boolean.opBoolean","SPLIT",FACE,{"disambiguationData":[TD([makeQuery(id+"F0lZXDNJsSuf2Zf_1.opExtrude","SWEPT_FACE",FACE,{"disambiguationData":[OSD([sQuery(id+"Fl6joLbU86pnRP5_1.wireOp",EDGE,"838e0230-e5e1-4c86-9a61-0dafe3e3d36a.sketch_text.stroke-0")])]})])],"derivedFrom":makeQuery(id+"F3.boolean.opBoolean","MERGE",FACE,{"derivedFrom":[makeQuery(id+"F1.opExtrude","SWEPT_FACE",FACE,{"disambiguationData":[OSD([subQ0])]}),makeQuery(id+"F3.opExtrude","SWEPT_FACE",FACE,{"disambiguationData":[OSD([subQ0])]})]})}),makeQuery(id+"F24.opExtrude","SWEPT_FACE",FACE,{"disambiguationData":[OSD([sQuery(id+"F23.wireOp",EDGE,"E74.left")])]})]});}
            var Q11;
            {var subQ0=sQuery(id+"F0.wireOp",EDGE,"E1");Q11=makeQuery(id+"F24.boolean.opBoolean","INTERSECT",EDGE,{"derivedFrom":[makeQuery(id+"F0lZXDNJsSuf2Zf_1.boolean.opBoolean","SPLIT",FACE,{"disambiguationData":[TD([makeQuery(id+"F0lZXDNJsSuf2Zf_1.opExtrude","SWEPT_FACE",FACE,{"disambiguationData":[OSD([sQuery(id+"Fl6joLbU86pnRP5_1.wireOp",EDGE,"838e0230-e5e1-4c86-9a61-0dafe3e3d36a.sketch_text.stroke-0")])]})])],"derivedFrom":makeQuery(id+"F3.boolean.opBoolean","MERGE",FACE,{"derivedFrom":[makeQuery(id+"F1.opExtrude","SWEPT_FACE",FACE,{"disambiguationData":[OSD([subQ0])]}),makeQuery(id+"F3.opExtrude","SWEPT_FACE",FACE,{"disambiguationData":[OSD([subQ0])]})]})}),makeQuery(id+"F24.opExtrude","SWEPT_FACE",FACE,{"disambiguationData":[OSD([sQuery(id+"F23.wireOp",EDGE,"E74.right")])]})]});}
            var Q12;
            {var subQ0=sQuery(id+"F0.wireOp",EDGE,"E1");Q12=makeQuery(id+"F24.boolean.opBoolean","INTERSECT",EDGE,{"disambiguationData":[OD(1.0)],"derivedFrom":[makeQuery(id+"F0lZXDNJsSuf2Zf_1.boolean.opBoolean","SPLIT",FACE,{"disambiguationData":[TD([makeQuery(id+"F0lZXDNJsSuf2Zf_1.opExtrude","SWEPT_FACE",FACE,{"disambiguationData":[OSD([sQuery(id+"Fl6joLbU86pnRP5_1.wireOp",EDGE,"838e0230-e5e1-4c86-9a61-0dafe3e3d36a.sketch_text.stroke-0")])]})])],"derivedFrom":makeQuery(id+"F3.boolean.opBoolean","MERGE",FACE,{"derivedFrom":[makeQuery(id+"F1.opExtrude","SWEPT_FACE",FACE,{"disambiguationData":[OSD([subQ0])]}),makeQuery(id+"F3.opExtrude","SWEPT_FACE",FACE,{"disambiguationData":[OSD([subQ0])]})]})}),makeQuery(id+"F24.opExtrude","CAP_FACE",FACE,{"disambiguationData":[OSD([sQuery(id+"F23.wireOp",EDGE,"E74.bottom"),sQuery(id+"F23.wireOp",EDGE,"E74.top"),sQuery(id+"F23.wireOp",EDGE,"E74.left"),sQuery(id+"F23.wireOp",EDGE,"E74.right")])],"isStart":false})]});}
            var Q13;
            {var subQ0=sQuery(id+"F0.wireOp",EDGE,"E1");Q13=makeQuery(id+"F24.boolean.opBoolean","INTERSECT",EDGE,{"disambiguationData":[OD(1.0)],"derivedFrom":[makeQuery(id+"F0lZXDNJsSuf2Zf_1.boolean.opBoolean","SPLIT",FACE,{"disambiguationData":[TD([makeQuery(id+"F0lZXDNJsSuf2Zf_1.opExtrude","SWEPT_FACE",FACE,{"disambiguationData":[OSD([sQuery(id+"Fl6joLbU86pnRP5_1.wireOp",EDGE,"838e0230-e5e1-4c86-9a61-0dafe3e3d36a.sketch_text.stroke-0")])]})])],"derivedFrom":makeQuery(id+"F3.boolean.opBoolean","MERGE",FACE,{"derivedFrom":[makeQuery(id+"F1.opExtrude","SWEPT_FACE",FACE,{"disambiguationData":[OSD([subQ0])]}),makeQuery(id+"F3.opExtrude","SWEPT_FACE",FACE,{"disambiguationData":[OSD([subQ0])]})]})}),makeQuery(id+"F24.opExtrude","CAP_FACE",FACE,{"disambiguationData":[OSD([sQuery(id+"F23.wireOp",EDGE,"E73.bottom"),sQuery(id+"F23.wireOp",EDGE,"E73.top"),sQuery(id+"F23.wireOp",EDGE,"E73.left"),sQuery(id+"F23.wireOp",EDGE,"E73.right")])],"isStart":false})]});}
            var Q14;
            {var subQ0=sQuery(id+"F0.wireOp",EDGE,"E1");Q14=makeQuery(id+"F24.boolean.opBoolean","INTERSECT",EDGE,{"disambiguationData":[OD(0.0)],"derivedFrom":[makeQuery(id+"F0lZXDNJsSuf2Zf_1.boolean.opBoolean","SPLIT",FACE,{"disambiguationData":[TD([makeQuery(id+"F0lZXDNJsSuf2Zf_1.opExtrude","SWEPT_FACE",FACE,{"disambiguationData":[OSD([sQuery(id+"Fl6joLbU86pnRP5_1.wireOp",EDGE,"838e0230-e5e1-4c86-9a61-0dafe3e3d36a.sketch_text.stroke-0")])]})])],"derivedFrom":makeQuery(id+"F3.boolean.opBoolean","MERGE",FACE,{"derivedFrom":[makeQuery(id+"F1.opExtrude","SWEPT_FACE",FACE,{"disambiguationData":[OSD([subQ0])]}),makeQuery(id+"F3.opExtrude","SWEPT_FACE",FACE,{"disambiguationData":[OSD([subQ0])]})]})}),makeQuery(id+"F24.opExtrude","CAP_FACE",FACE,{"disambiguationData":[OSD([sQuery(id+"F23.wireOp",EDGE,"E73.bottom"),sQuery(id+"F23.wireOp",EDGE,"E73.top"),sQuery(id+"F23.wireOp",EDGE,"E73.left"),sQuery(id+"F23.wireOp",EDGE,"E73.right")])],"isStart":false})]});}
            var Q15;
            {var subQ0=sQuery(id+"F0.wireOp",EDGE,"E1");Q15=makeQuery(id+"F24.boolean.opBoolean","INTERSECT",EDGE,{"disambiguationData":[OD(0.0)],"derivedFrom":[makeQuery(id+"F0lZXDNJsSuf2Zf_1.boolean.opBoolean","SPLIT",FACE,{"disambiguationData":[TD([makeQuery(id+"F0lZXDNJsSuf2Zf_1.opExtrude","SWEPT_FACE",FACE,{"disambiguationData":[OSD([sQuery(id+"Fl6joLbU86pnRP5_1.wireOp",EDGE,"838e0230-e5e1-4c86-9a61-0dafe3e3d36a.sketch_text.stroke-0")])]})])],"derivedFrom":makeQuery(id+"F3.boolean.opBoolean","MERGE",FACE,{"derivedFrom":[makeQuery(id+"F1.opExtrude","SWEPT_FACE",FACE,{"disambiguationData":[OSD([subQ0])]}),makeQuery(id+"F3.opExtrude","SWEPT_FACE",FACE,{"disambiguationData":[OSD([subQ0])]})]})}),makeQuery(id+"F24.opExtrude","CAP_FACE",FACE,{"disambiguationData":[OSD([sQuery(id+"F23.wireOp",EDGE,"E74.bottom"),sQuery(id+"F23.wireOp",EDGE,"E74.top"),sQuery(id+"F23.wireOp",EDGE,"E74.left"),sQuery(id+"F23.wireOp",EDGE,"E74.right")])],"isStart":false})]});}
            chamfer(context, id + "F30", {"entities" : qUnion([Q0, Q1, Q2, Q3, Q4, Q5, Q6, Q7, Q8, Q9, Q10, Q11, Q12, Q13, Q14, Q15]), "width" : .25 * mm, "tangentPropagation" : true});
        }
        {
            var Q0;
            Q0=qCreatedBy(makeId("Right.planeOp"),FACE);
            var sketch = newSketch(context, id + "F31", { "sketchPlane" : qUnion([Q0])});
            skLineSegment(sketch, "E78", {"start": v(-1.75, -7.44) * mm, "end": v(-1.75, -8.44) * mm});
            skLineSegment(sketch, "E79", {"start": v(-1.75, -7.94) * mm, "end": v(-0.75, -7.94) * mm});
            skLineSegment(sketch, "E80", {"start": v(-0.75, -7.94) * mm, "end": v(-1.75, -7.44) * mm});
            skLineSegment(sketch, "E81", {"start": v(-0.75, -7.94) * mm, "end": v(-1.75, -8.44) * mm});
            skLineSegment(sketch, "E82", {"start": v(-1.75, 8.44) * mm, "end": v(-1.75, 7.44) * mm});
            skLineSegment(sketch, "E83", {"start": v(-1.75, 7.94) * mm, "end": v(-0.75, 7.94) * mm});
            skLineSegment(sketch, "E84", {"start": v(-0.75, 7.94) * mm, "end": v(-1.75, 7.44) * mm});
            skLineSegment(sketch, "E85", {"start": v(-1.75, 8.44) * mm, "end": v(-0.75, 7.94) * mm});
            skSolve(sketch);
        }
        {
            var Q0;
            {var subQ2=sQuery(id+"F31.wireOp",EDGE,"E79");Q0=makeQuery(id+"F31.imprint","IMPRINT",FACE,{"disambiguationData":[TD([[makeQuery(id+"F31.imprint","IMPRINT",EDGE,{"derivedFrom":subQ2}),-1.0]])]});}
            var Q1;
            {var subQ2=sQuery(id+"F31.wireOp",EDGE,"E79");Q1=makeQuery(id+"F31.imprint","IMPRINT",FACE,{"disambiguationData":[TD([[makeQuery(id+"F31.imprint","IMPRINT",EDGE,{"derivedFrom":subQ2}),1.0]])]});}
            var Q2;
            {var subQ2=sQuery(id+"F31.wireOp",EDGE,"E83");Q2=makeQuery(id+"F31.imprint","IMPRINT",FACE,{"disambiguationData":[TD([[makeQuery(id+"F31.imprint","IMPRINT",EDGE,{"derivedFrom":subQ2}),1.0]])]});}
            var Q3;
            {var subQ2=sQuery(id+"F31.wireOp",EDGE,"E83");Q3=makeQuery(id+"F31.imprint","IMPRINT",FACE,{"disambiguationData":[TD([[makeQuery(id+"F31.imprint","IMPRINT",EDGE,{"derivedFrom":subQ2}),-1.0]])]});}
            extrude(context, id + "F32", {"entities" : qUnion([Q0, Q1, Q2, Q3]), "operationType" : NewBodyOperationType.REMOVE, "depth" : 10 * mm, "offsetDistance" : 25 * mm, "hasSecondDirection" : true, "secondDirectionOppositeDirection" : true, "secondDirectionDepth" : 10 * mm});
        }
        {
            var Q0;
            {var subQ0=sQuery(id+"F4.wireOp",EDGE,"E12");Q0=makeQuery(id+"F32.boolean.opBoolean","SPLIT",FACE,{"disambiguationData":[TD([makeQuery(id+"F2.opExtrude","SWEPT_FACE",FACE,{"disambiguationData":[OSD([sQuery(id+"F0.wireOp",EDGE,"E4")])]}),makeQuery(id+"F5.boolean.opBoolean","COPY",FACE,{"derivedFrom":makeQuery(id+"F5.opExtrude","SWEPT_FACE",FACE,{"disambiguationData":[OSD([subQ0])]})}),makeQuery(id+"F40.boolean.opBoolean","COPY",FACE,{"derivedFrom":makeQuery(id+"F40.opExtrude","SWEPT_FACE",FACE,{"disambiguationData":[OSD([sQuery(id+"F10.wireOp",EDGE,"E43.top")])]})}),makeQuery(id+"F40.boolean.opBoolean","COPY",FACE,{"derivedFrom":makeQuery(id+"F40.opExtrude","SWEPT_FACE",FACE,{"disambiguationData":[OSD([sQuery(id+"F10.wireOp",EDGE,"E43.left")])]})}),makeQuery(id+"F32.opExtrude","SWEPT_FACE",FACE,{"disambiguationData":[OSD([sQuery(id+"F31.wireOp",EDGE,"E85")])]})])],"derivedFrom":makeQuery(id+"F5.boolean.opBoolean","COPY",FACE,{"derivedFrom":makeQuery(id+"F5.opExtrude","CAP_FACE",FACE,{"disambiguationData":[OSD([subQ0])],"isStart":false})})});}
            var sketch = newSketch(context, id + "F33", { "sketchPlane" : qUnion([Q0])});
            skLineSegment(sketch, "E86.bottom", {"start": v(8.07, 7.9) * mm, "end": v(-8.07, 7.9) * mm});
            skLineSegment(sketch, "E86.top", {"start": v(8.07, -7.9) * mm, "end": v(-8.07, -7.9) * mm});
            skLineSegment(sketch, "E86.left", {"start": v(8.07, 7.9) * mm, "end": v(8.07, -7.9) * mm});
            skLineSegment(sketch, "E86.right", {"start": v(-8.07, 7.9) * mm, "end": v(-8.07, -7.9) * mm});
            skPoint(sketch, "E86.middle", {"position": v(0, 0) * mm});
            skSolve(sketch);
        }
        {
            var Q0;
            Q0 = qSketchRegion(id + "F33", true);
            extrude(context, id + "F34", {"entities" : qUnion([Q0]), "operationType" : NewBodyOperationType.REMOVE, "depth" : 25 * mm, "offsetDistance" : 25 * mm});
        }
        {
            var Q0;
            {var subQ0=sQuery(id+"FWxMzrt1rZLhw1a_1.wireOp",EDGE,"1z2TxVRK-6zxj-oHG3-mA6c-GiNbkqZBGqNg.top");var subQ1=sQuery(id+"F6.wireOp",EDGE,"E15");var subQ2=makeQuery(id+"F7.opExtrude","CAP_EDGE",EDGE,{"disambiguationData":[OSD([subQ1])],"isStart":false});var subQ3=makeQuery(id+"FWxMzrt1rZLhw1a_1.imprint","INTERSECT",VERTEX,{"derivedFrom":[subQ2,subQ0]});var subQ4=sQuery(id+"F6.wireOp",EDGE,"E14");var subQ6=sQuery(id+"F6.wireOp",EDGE,"E23.MirrorCS");var subQ10=sQuery(id+"F6.wireOp",EDGE,"E17");Q0=makeQuery(id+"F8uPzhW09N0M85Q_1.boolean.opBoolean","SPLIT",FACE,{"disambiguationData":[TD([makeQuery(id+"F8uPzhW09N0M85Q_1.opExtrude","SWEPT_FACE",FACE,{"disambiguationData":[OSD([subQ0]),TDD([makeQuery(id+"FWxMzrt1rZLhw1a_1.imprint","IMPRINT",EDGE,{"disambiguationData":[TD([[subQ3,1.0]])],"derivedFrom":subQ0}),makeQuery(id+"FWxMzrt1rZLhw1a_1.imprint","IMPRINT",EDGE,{"disambiguationData":[TD([[makeQuery(id+"FWxMzrt1rZLhw1a_1.imprint","INTERSECT",VERTEX,{"derivedFrom":[subQ0,sQuery(id+"FWxMzrt1rZLhw1a_1.wireOp",EDGE,"78RMPhYd-id3w-eDH9-Um3x-JQcaQHo3oXG0")]}),1.0]])],"derivedFrom":subQ0})])]})])],"derivedFrom":makeQuery(id+"F7.opExtrude","CAP_FACE",FACE,{"disambiguationData":[OSD([subQ4,subQ1,subQ10,subQ6])],"isStart":false})});}
            var sketch = newSketch(context, id + "F35", { "sketchPlane" : qUnion([Q0])});
            skLineSegment(sketch, "E87", {"start": v(0, 0) * mm, "end": v(5.4, 0) * mm});
            skPoint(sketch, "E88.endSnap0", {"position": v(0, 18.5) * mm});
            skCircle(sketch, "E89", {"center": v(0, 16) * mm, "radius": 2.5 * mm});
            skPoint(sketch, "E90", {"position": v(2.7, 17.29) * mm});
            skPoint(sketch, "E91", {"position": v(-2.7, 17.29) * mm});
            skLineSegment(sketch, "E92", {"start": v(-2.7, 17.29) * mm, "end": v(-2.96, 19.08) * mm});
            skLineSegment(sketch, "E93", {"start": v(2.7, 17.29) * mm, "end": v(2.93, 18.72) * mm});
            skLineSegment(sketch, "E94", {"start": v(-2.7, 17.29) * mm, "end": v(-2.4, 16.7) * mm});
            skLineSegment(sketch, "E95", {"start": v(2.7, 17.29) * mm, "end": v(2.38, 16.76) * mm});
            skLineSegment(sketch, "E96", {"start": v(-2.96, 19.08) * mm, "end": v(2.93, 18.72) * mm});
            skPoint(sketch, "E97.trimOffspring.end.orphan", {"position": v(0, 20.47) * mm});
            skLineSegment(sketch, "E98.MirrorCS", {"start": v(-2.7, -17.29) * mm, "end": v(-2.4, -16.7) * mm});
            skLineSegment(sketch, "E99.MirrorCS", {"start": v(2.7, -17.29) * mm, "end": v(2.38, -16.76) * mm});
            skLineSegment(sketch, "E100.MirrorCS", {"start": v(2.7, -17.29) * mm, "end": v(2.93, -18.72) * mm});
            skPoint(sketch, "E101.MirrorP", {"position": v(-2.7, -17.29) * mm});
            skPoint(sketch, "E102.MirrorP", {"position": v(0, -18.5) * mm});
            skPoint(sketch, "E103.MirrorP", {"position": v(2.7, -17.29) * mm});
            skLineSegment(sketch, "E104.MirrorCS", {"start": v(-2.96, -19.08) * mm, "end": v(2.93, -18.72) * mm});
            skLineSegment(sketch, "E105.MirrorCS", {"start": v(-2.7, -17.29) * mm, "end": v(-2.96, -19.08) * mm});
            skCircle(sketch, "E106.MirrorC", {"center": v(0, -16) * mm, "radius": 2.5 * mm});
            skSolve(sketch);
        }
        {
            var Q0;
            Q0=makeQuery(id+"F9.opExtrude","SWEPT_EDGE",EDGE,{"disambiguationData":[OSD([sQuery(id+"F8.wireOp",EDGE,"E34.bottom"),sQuery(id+"F8.wireOp",EDGE,"E34.right"),sQuery(id+"F8.wireOp",EDGE,"E37.MirrorCS")])]});
            var Q1;
            Q1=makeQuery(id+"F9.opExtrude","SWEPT_EDGE",EDGE,{"disambiguationData":[OSD([sQuery(id+"F8.wireOp",EDGE,"E34.bottom"),sQuery(id+"F8.wireOp",EDGE,"E34.left")])]});
            var Q2;
            Q2=makeQuery(id+"F9.opExtrude","SWEPT_EDGE",EDGE,{"disambiguationData":[OSD([sQuery(id+"F8.wireOp",EDGE,"E39.MirrorCS"),sQuery(id+"F8.wireOp",EDGE,"E41.MirrorCS")])]});
            var Q3;
            Q3=makeQuery(id+"F9.opExtrude","SWEPT_EDGE",EDGE,{"disambiguationData":[OSD([sQuery(id+"F8.wireOp",EDGE,"E40.MirrorCS"),sQuery(id+"F8.wireOp",EDGE,"E41.MirrorCS")])]});
            var Q4;
            Q4=makeQuery(id+"F9.opExtrude","CAP_EDGE",EDGE,{"disambiguationData":[OSD([sQuery(id+"F8.wireOp",EDGE,"E34.bottom")])],"isStart":false});
            var Q5;
            Q5=makeQuery(id+"F9.opExtrude","CAP_EDGE",EDGE,{"disambiguationData":[OSD([sQuery(id+"F8.wireOp",EDGE,"E41.MirrorCS")])],"isStart":false});
            chamfer(context, id + "F36", {"entities" : qUnion([Q0, Q1, Q2, Q3, Q4, Q5]), "width" : 1 * mm, "tangentPropagation" : true});
        }
        {
            var Q0;
            {var subQ0=sQuery(id+"F0.wireOp",EDGE,"E1");Q0=makeQuery(id+"F18.boolean.opBoolean","INTERSECT",EDGE,{"derivedFrom":[makeQuery(id+"F3.boolean.opBoolean","MERGE",FACE,{"derivedFrom":[makeQuery(id+"F1.opExtrude","SWEPT_FACE",FACE,{"disambiguationData":[OSD([subQ0])]}),makeQuery(id+"F3.opExtrude","SWEPT_FACE",FACE,{"disambiguationData":[OSD([subQ0])]})]}),makeQuery(id+"F18.opExtrude","SWEPT_FACE",FACE,{"disambiguationData":[OSD([sQuery(id+"F17.wireOp",EDGE,"E67")])]})]});}
            var Q1;
            {var subQ0=sQuery(id+"F0.wireOp",EDGE,"E1");Q1=makeQuery(id+"F18.boolean.opBoolean","INTERSECT",EDGE,{"derivedFrom":[makeQuery(id+"F3.boolean.opBoolean","MERGE",FACE,{"derivedFrom":[makeQuery(id+"F1.opExtrude","SWEPT_FACE",FACE,{"disambiguationData":[OSD([subQ0])]}),makeQuery(id+"F3.opExtrude","SWEPT_FACE",FACE,{"disambiguationData":[OSD([subQ0])]})]}),makeQuery(id+"F18.opExtrude","SWEPT_FACE",FACE,{"disambiguationData":[OSD([sQuery(id+"F17.wireOp",EDGE,"E65")])]})]});}
            var Q2;
            {var subQ0=sQuery(id+"F0.wireOp",EDGE,"E1");Q2=makeQuery(id+"F21.boolean.opBoolean","INTERSECT",EDGE,{"derivedFrom":[makeQuery(id+"F3.boolean.opBoolean","MERGE",FACE,{"derivedFrom":[makeQuery(id+"F1.opExtrude","SWEPT_FACE",FACE,{"disambiguationData":[OSD([subQ0])]}),makeQuery(id+"F3.opExtrude","SWEPT_FACE",FACE,{"disambiguationData":[OSD([subQ0])]})]}),makeQuery(id+"F21.opExtrude","SWEPT_FACE",FACE,{"disambiguationData":[OSD([sQuery(id+"F20.wireOp",EDGE,"E69")])]})]});}
            var Q3;
            {var subQ0=sQuery(id+"F0.wireOp",EDGE,"E1");Q3=makeQuery(id+"F21.boolean.opBoolean","INTERSECT",EDGE,{"derivedFrom":[makeQuery(id+"F3.boolean.opBoolean","MERGE",FACE,{"derivedFrom":[makeQuery(id+"F1.opExtrude","SWEPT_FACE",FACE,{"disambiguationData":[OSD([subQ0])]}),makeQuery(id+"F3.opExtrude","SWEPT_FACE",FACE,{"disambiguationData":[OSD([subQ0])]})]}),makeQuery(id+"F21.opExtrude","SWEPT_FACE",FACE,{"disambiguationData":[OSD([sQuery(id+"F20.wireOp",EDGE,"E71")])]})]});}
            chamfer(context, id + "F37", {"entities" : qUnion([Q0, Q1, Q2, Q3]), "width" : .25 * mm, "tangentPropagation" : true});
        }
        {
            var Q0;
            Q0=makeQuery(id+"F1.opExtrude","CAP_EDGE",EDGE,{"disambiguationData":[OSD([sQuery(id+"F0.wireOp",EDGE,"E11")])],"isStart":false});
            chamfer(context, id + "F38", {"entities" : qUnion([Q0]), "chamferType" : ChamferType.TWO_OFFSETS, "width1" : .75 * mm, "oppositeDirection" : false, "width2" : .55 * mm, "tangentPropagation" : true});
        }
        {
            var Q0;
            {var subQ0=sQuery(id+"F35.wireOp",EDGE,"E89");var subQ7=makeQuery(id+"F35.imprint","INTERSECT",VERTEX,{"derivedFrom":[subQ0,sQuery(id+"F35.wireOp",EDGE,"E94")]});Q0=makeQuery(id+"F35.imprint","IMPRINT",FACE,{"disambiguationData":[TD([[makeQuery(id+"F35.imprint","IMPRINT",EDGE,{"disambiguationData":[TD([[subQ7,-1.0]])],"derivedFrom":subQ0}),1.0]])]});}
            var Q1;
            {var subQ0=sQuery(id+"F35.wireOp",EDGE,"E89");var subQ6=makeQuery(id+"F35.imprint","INTERSECT",VERTEX,{"derivedFrom":[makeQuery(id+"F7.opExtrude","CAP_EDGE",EDGE,{"disambiguationData":[OSD([sQuery(id+"F6.wireOp",EDGE,"E15")])],"isStart":false}),subQ0]});Q1=makeQuery(id+"F35.imprint","IMPRINT",FACE,{"disambiguationData":[TD([[makeQuery(id+"F35.imprint","IMPRINT",EDGE,{"disambiguationData":[TD([[subQ6,1.0]])],"derivedFrom":subQ0}),1.0]])]});}
            var Q2;
            {var subQ1=makeQuery(id+"F7.opExtrude","CAP_EDGE",EDGE,{"disambiguationData":[OSD([sQuery(id+"F6.wireOp",EDGE,"E15")])],"isStart":false});var subQ8=sQuery(id+"F35.wireOp",EDGE,"E92");var subQ10=makeQuery(id+"F35.imprint","INTERSECT",VERTEX,{"derivedFrom":[subQ1,subQ8]});Q2=makeQuery(id+"F35.imprint","IMPRINT",FACE,{"disambiguationData":[TD([[makeQuery(id+"F35.imprint","IMPRINT",EDGE,{"disambiguationData":[TD([[subQ10,1.0]])],"derivedFrom":subQ1}),1.0]])]});}
            var Q3;
            {var subQ6=makeQuery(id+"F7.opExtrude","CAP_EDGE",EDGE,{"disambiguationData":[OSD([sQuery(id+"F6.wireOp",EDGE,"E15")])],"isStart":false});var subQ8=sQuery(id+"F35.wireOp",EDGE,"E93");var subQ10=makeQuery(id+"F35.imprint","INTERSECT",VERTEX,{"derivedFrom":[subQ6,subQ8]});Q3=makeQuery(id+"F35.imprint","IMPRINT",FACE,{"disambiguationData":[TD([[makeQuery(id+"F35.imprint","IMPRINT",EDGE,{"disambiguationData":[TD([[subQ10,-1.0]])],"derivedFrom":subQ6}),1.0]])]});}
            var Q4;
            {var subQ1=sQuery(id+"F35.wireOp",EDGE,"E98.MirrorCS");Q4=makeQuery(id+"F35.imprint","IMPRINT",FACE,{"disambiguationData":[TD([[makeQuery(id+"F35.imprint","IMPRINT",EDGE,{"derivedFrom":subQ1}),-1.0]])]});}
            var Q5;
            {var subQ0=sQuery(id+"F35.wireOp",EDGE,"E106.MirrorC");var subQ1=makeQuery(id+"F35.imprint","INTERSECT",VERTEX,{"derivedFrom":[sQuery(id+"F35.wireOp",EDGE,"E98.MirrorCS"),subQ0]});Q5=makeQuery(id+"F35.imprint","IMPRINT",FACE,{"disambiguationData":[TD([[makeQuery(id+"F35.imprint","IMPRINT",EDGE,{"disambiguationData":[TD([[subQ1,1.0]])],"derivedFrom":subQ0}),-1.0]])]});}
            extrude(context, id + "F39", {"entities" : qUnion([Q0, Q1, Q2, Q3, Q4, Q5]), "operationType" : NewBodyOperationType.REMOVE, "oppositeDirection" : true, "depth" : 4 * mm, "offsetDistance" : 25 * mm});
        }
        {
            var Q0;
            {var subQ0=sQuery(id+"F0.wireOp",EDGE,"E3.top");var subQ1=makeQuery(id+"F2.opExtrude","CAP_EDGE",EDGE,{"disambiguationData":[OSD([subQ0])],"isStart":false});Q0=makeQuery(id+"F10.imprint","IMPRINT",FACE,{"disambiguationData":[TD([[makeQuery(id+"F10.imprint","IMPRINT",EDGE,{"derivedFrom":subQ1}),1.0]])]});}
            var Q1;
            {var subQ4=sQuery(id+"F0.wireOp",EDGE,"E3.right");var subQ7=makeQuery(id+"F2.opExtrude","CAP_EDGE",EDGE,{"disambiguationData":[OSD([subQ4])],"isStart":false});Q1=makeQuery(id+"F10.imprint","IMPRINT",FACE,{"disambiguationData":[TD([[makeQuery(id+"F10.imprint","IMPRINT",EDGE,{"derivedFrom":subQ7}),1.0]])]});}
            var Q2;
            {var subQ2=sQuery(id+"F0.wireOp",EDGE,"E3.top");var subQ7=makeQuery(id+"F2.opExtrude","CAP_EDGE",EDGE,{"disambiguationData":[OSD([subQ2])],"isStart":false});Q2=makeQuery(id+"F10.imprint","IMPRINT",FACE,{"disambiguationData":[TD([[makeQuery(id+"F10.imprint","IMPRINT",EDGE,{"derivedFrom":subQ7}),-1.0]])]});}
            var Q3;
            {var subQ4=sQuery(id+"F0.wireOp",EDGE,"E3.bottom");var subQ7=makeQuery(id+"F2.opExtrude","CAP_EDGE",EDGE,{"disambiguationData":[OSD([subQ4])],"isStart":false});Q3=makeQuery(id+"F10.imprint","IMPRINT",FACE,{"disambiguationData":[TD([[makeQuery(id+"F10.imprint","IMPRINT",EDGE,{"derivedFrom":subQ7}),1.0]])]});}
            var Q4;
            {var subQ2=sQuery(id+"F0.wireOp",EDGE,"E3.left");var subQ7=makeQuery(id+"F2.opExtrude","CAP_EDGE",EDGE,{"disambiguationData":[OSD([subQ2])],"isStart":false});Q4=makeQuery(id+"F10.imprint","IMPRINT",FACE,{"disambiguationData":[TD([[makeQuery(id+"F10.imprint","IMPRINT",EDGE,{"derivedFrom":subQ7}),-1.0]])]});}
            extrude(context, id + "F40", {"entities" : qUnion([Q0, Q1, Q2, Q3, Q4]), "operationType" : NewBodyOperationType.REMOVE, "oppositeDirection" : true, "depth" : 25 * mm, "offsetDistance" : 25 * mm});
        }
        {
            var Q0;
            {var subQ0=sQuery(id+"F35.wireOp",EDGE,"E89");var subQ6=makeQuery(id+"F35.imprint","INTERSECT",VERTEX,{"derivedFrom":[makeQuery(id+"F7.opExtrude","CAP_EDGE",EDGE,{"disambiguationData":[OSD([sQuery(id+"F6.wireOp",EDGE,"E15")])],"isStart":false}),subQ0]});Q0=makeQuery(id+"F35.imprint","IMPRINT",FACE,{"disambiguationData":[TD([[makeQuery(id+"F35.imprint","IMPRINT",EDGE,{"disambiguationData":[TD([[subQ6,1.0]])],"derivedFrom":subQ0}),1.0]])]});}
            var Q1;
            {var subQ0=sQuery(id+"F35.wireOp",EDGE,"E106.MirrorC");var subQ1=makeQuery(id+"F35.imprint","INTERSECT",VERTEX,{"derivedFrom":[sQuery(id+"F35.wireOp",EDGE,"E98.MirrorCS"),subQ0]});Q1=makeQuery(id+"F35.imprint","IMPRINT",FACE,{"disambiguationData":[TD([[makeQuery(id+"F35.imprint","IMPRINT",EDGE,{"disambiguationData":[TD([[subQ1,1.0]])],"derivedFrom":subQ0}),-1.0]])]});}
            var Q2;
            {var subQ0=sQuery(id+"F35.wireOp",EDGE,"E89");var subQ8=makeQuery(id+"F35.imprint","INTERSECT",VERTEX,{"derivedFrom":[subQ0,sQuery(id+"F35.wireOp",EDGE,"E94")]});Q2=makeQuery(id+"F35.imprint","IMPRINT",FACE,{"disambiguationData":[TD([[makeQuery(id+"F35.imprint","IMPRINT",EDGE,{"disambiguationData":[TD([[subQ8,-1.0]])],"derivedFrom":subQ0}),1.0]])]});}
            extrude(context, id + "F41", {"entities" : qUnion([Q0, Q1, Q2]), "operationType" : NewBodyOperationType.REMOVE, "oppositeDirection" : true, "depth" : 25 * mm, "offsetDistance" : 25 * mm});
        }
    });
